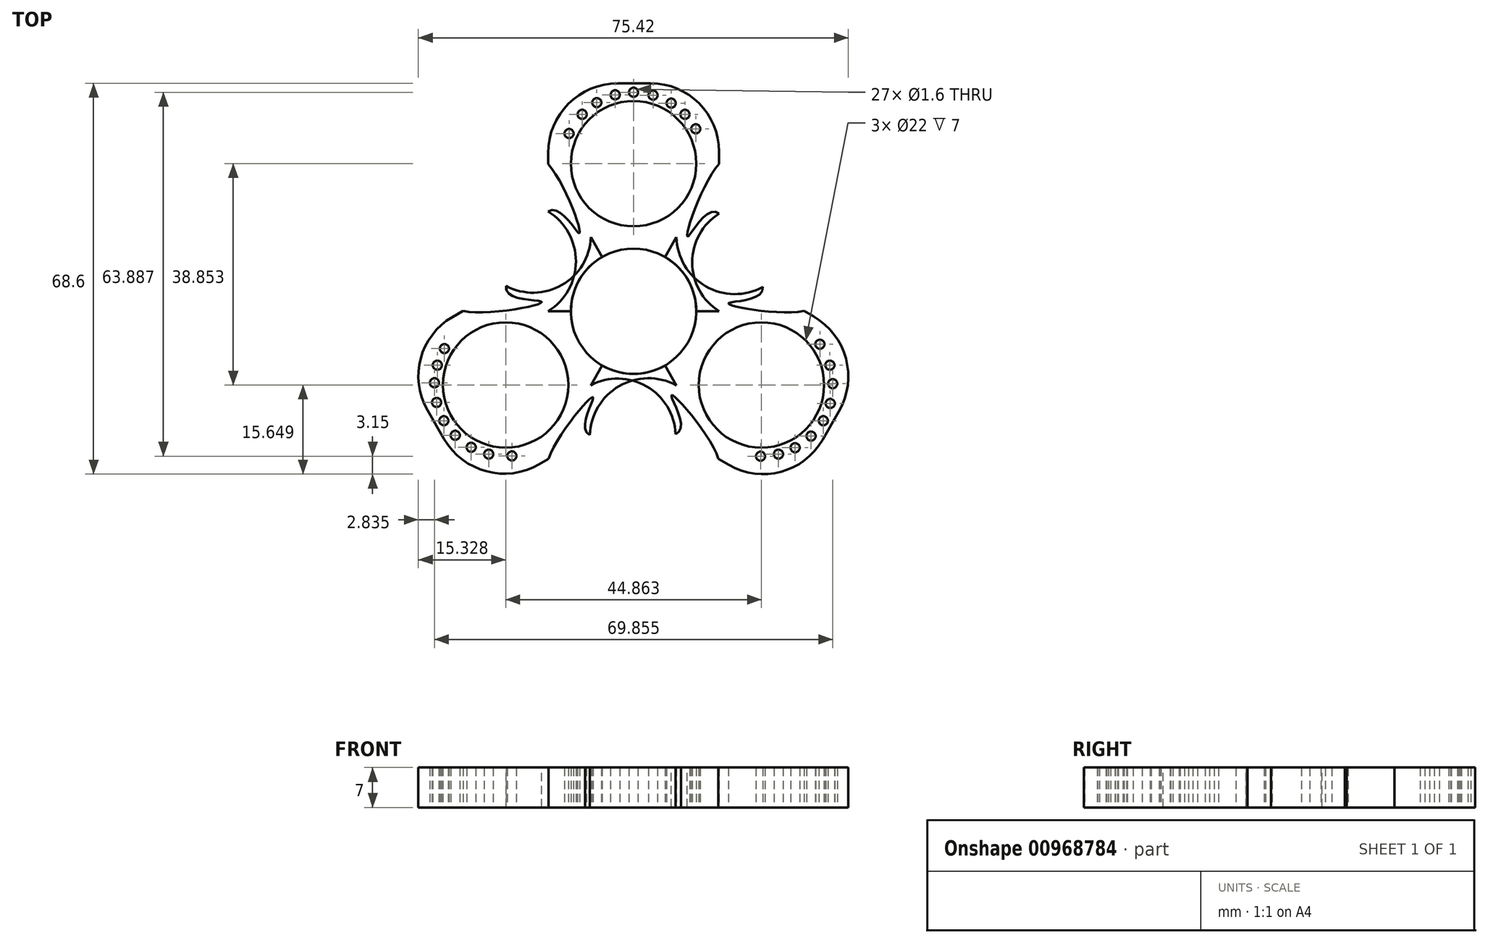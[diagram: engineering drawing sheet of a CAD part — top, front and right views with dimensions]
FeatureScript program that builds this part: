
annotation { "Feature Type Name" : "Feature", "Feature Type Description" : "" }
export const myFeature = defineFeature(function(context is Context, id is Id, definition is map)
    precondition{}
    {
        {
            var Q0;
            Q0=qCreatedBy(makeId("Top.planeOp"),FACE);
            var sketch = newSketch(context, id + "F0", { "sketchPlane" : qUnion([Q0])});
            skCircle(sketch, "E0", {"center": v(0, 0) * mm, "radius": 11 * mm});
            skLineSegment(sketch, "E1.bottom", {"start": v(0, 0) * mm, "end": v(15, 0) * mm});
            skLineSegment(sketch, "E1.top", {"start": v(0, 40) * mm, "end": v(3.02, 40) * mm});
            skLineSegment(sketch, "E1.left", {"start": v(0, 0) * mm, "end": v(0, 40) * mm});
            skLineSegment(sketch, "E1.right", {"start": v(15, 0) * mm, "end": v(15, 28.02) * mm});
            skLineSegment(sketch, "E2.bottom", {"start": v(0, 0) * mm, "end": v(-15, 0) * mm});
            skLineSegment(sketch, "E2.top", {"start": v(0, 40) * mm, "end": v(-2.77, 40) * mm});
            skLineSegment(sketch, "E2.right", {"start": v(-15, 0) * mm, "end": v(-15, 27.77) * mm});
            skLineSegment(sketch, "E3", {"start": v(0, 40) * mm, "end": v(0, 25.9) * mm});
            skCircle(sketch, "E4", {"center": v(0, 25.9) * mm, "radius": 11 * mm});
            skPoint(sketch, "E5.visualSharp", {"position": v(-15, 40) * mm});
            skArc(sketch, "E5.filletArc", {"start": v(-2.77, 40) * mm, "mid": v(-11.42, 36.42) * mm, "end": v(-15, 27.77) * mm});
            skPoint(sketch, "E6.visualSharp", {"position": v(15, 40) * mm});
            skArc(sketch, "E6.filletArc", {"start": v(15, 28.02) * mm, "mid": v(11.5, 36.5) * mm, "end": v(3.02, 40) * mm});
            skPoint(sketch, "E7.1.internal.snap0", {"position": v(-15, 13.88) * mm});
            skFitSpline(sketch, "E8", {"points": [v(-15, 25.86) * mm, v(-9.57, 13.73) * mm, v(-15, 17.51) * mm], "startDerivative": vector(15.03, -16.72) * mm, "endDerivative": vector(-15.82, -9.96) * mm});
            skFitSpline(sketch, "E9", {"points": [v(15, 25.86) * mm, v(9.53, 13.16) * mm, v(15, 17.15) * mm], "startDerivative": vector(-14.64, -15.58) * mm, "endDerivative": vector(14.98, -12.69) * mm});
            skPoint(sketch, "E10", {"position": v(15, 14) * mm});
            skCircle(sketch, "E11", {"center": v(-11.32, 31.2) * mm, "radius": 0.8 * mm});
            skCircle(sketch, "E12", {"center": v(-9.02, 34.56) * mm, "radius": 0.8 * mm});
            skCircle(sketch, "E13", {"center": v(-6.44, 36.61) * mm, "radius": 0.8 * mm});
            skCircle(sketch, "E14", {"center": v(-3.23, 37.98) * mm, "radius": 0.8 * mm});
            skCircle(sketch, "E15", {"center": v(0, 38.44) * mm, "radius": 0.8 * mm});
            skCircle(sketch, "E16", {"center": v(3.41, 37.93) * mm, "radius": 0.8 * mm});
            skCircle(sketch, "E17", {"center": v(6.6, 36.52) * mm, "radius": 0.8 * mm});
            skCircle(sketch, "E18", {"center": v(9.02, 34.56) * mm, "radius": 0.8 * mm});
            skCircle(sketch, "E19", {"center": v(10.9, 32.02) * mm, "radius": 0.8 * mm});
            skArc(sketch, "E20", {"start": v(-15, 0) * mm, "mid": v(-10.12, 8.76) * mm, "end": v(-15, 17.51) * mm});
            skArc(sketch, "E21", {"start": v(15, 17.15) * mm, "mid": v(10.27, 8.57) * mm, "end": v(15, 0) * mm});
            skLineSegment(sketch, "E22", {"start": v(-11.32, 31.2) * mm, "end": v(0, 25.9) * mm, "construction": true});
            skLineSegment(sketch, "E23", {"start": v(-9.02, 34.56) * mm, "end": v(0, 25.9) * mm, "construction": true});
            skLineSegment(sketch, "E24", {"start": v(-6.44, 36.61) * mm, "end": v(0, 25.9) * mm, "construction": true});
            skLineSegment(sketch, "E25", {"start": v(-3.23, 37.98) * mm, "end": v(0, 25.9) * mm, "construction": true});
            skLineSegment(sketch, "E26", {"start": v(0, 38.44) * mm, "end": v(0, 25.9) * mm});
            skLineSegment(sketch, "E27", {"start": v(3.41, 37.93) * mm, "end": v(0, 25.9) * mm, "construction": true});
            skLineSegment(sketch, "E28", {"start": v(6.6, 36.52) * mm, "end": v(0, 25.9) * mm, "construction": true});
            skLineSegment(sketch, "E29", {"start": v(9.02, 34.56) * mm, "end": v(0, 25.9) * mm, "construction": true});
            skLineSegment(sketch, "E30", {"start": v(10.9, 32.02) * mm, "end": v(0, 25.9) * mm, "construction": true});
            skSolve(sketch);
        }
        {
            var Q0;
            {var subQ0=sQuery(id+"F0.wireOp",EDGE,"E2.top");Q0=makeQuery(id+"F0.imprint","IMPRINT",FACE,{"disambiguationData":[TD([[makeQuery(id+"F0.imprint","IMPRINT",EDGE,{"derivedFrom":subQ0}),1.0]])]});}
            var Q1;
            {var subQ9=sQuery(id+"F0.wireOp",EDGE,"E1.top");Q1=makeQuery(id+"F0.imprint","IMPRINT",FACE,{"disambiguationData":[TD([[makeQuery(id+"F0.imprint","IMPRINT",EDGE,{"derivedFrom":subQ9}),-1.0]])]});}
            extrude(context, id + "F1", {"entities" : qUnion([Q0, Q1]), "depth" : 7 * mm, "offsetDistance" : 25 * mm});
        }
        {
            var Q0;
            Q0=qCreatedBy(makeId("Front.planeOp"),FACE);
            var sketch = newSketch(context, id + "F2", { "sketchPlane" : qUnion([Q0])});
            skLineSegment(sketch, "E31", {"start": v(0, 0) * mm, "end": v(0, 68.14) * mm});
            skSolve(sketch);
        }
        {
            var Q0;
            Q0=makeQuery(id+"F1.opExtrude","SWEPT_BODY",BODY,{"disambiguationData":[OSD([sQuery(id+"F0.wireOp",EDGE,"E0"),sQuery(id+"F0.wireOp",EDGE,"E1.bottom"),sQuery(id+"F0.wireOp",EDGE,"E1.top"),sQuery(id+"F0.wireOp",EDGE,"E1.right"),sQuery(id+"F0.wireOp",EDGE,"E2.bottom"),sQuery(id+"F0.wireOp",EDGE,"E2.top"),sQuery(id+"F0.wireOp",EDGE,"E2.right"),sQuery(id+"F0.wireOp",EDGE,"E4")])]});
            var Q1;
            Q1=sQuery(id+"F2.wireOp",EDGE,"E31");
            var Q2;
            Q2=sQuery(id+"F2.wireOp",EDGE,"E31");
            transform(context, id + "F3", {"entities" : qUnion([Q0]), "transformType" : TransformType.ROTATION, "transformAxis" : qUnion([Q2]), "angle" : 120 * degree, "makeCopy" : true});
        }
        {
            var Q0;
            Q0=makeQuery(id+"F3.opPattern","COPY",BODY,{"derivedFrom":makeQuery(id+"F1.opExtrude","SWEPT_BODY",BODY,{"disambiguationData":[OSD([sQuery(id+"F0.wireOp",EDGE,"E0"),sQuery(id+"F0.wireOp",EDGE,"E1.bottom"),sQuery(id+"F0.wireOp",EDGE,"E1.top"),sQuery(id+"F0.wireOp",EDGE,"E1.right"),sQuery(id+"F0.wireOp",EDGE,"E2.bottom"),sQuery(id+"F0.wireOp",EDGE,"E2.top"),sQuery(id+"F0.wireOp",EDGE,"E2.right"),sQuery(id+"F0.wireOp",EDGE,"E4")])]}),"instanceName":"1"});
            var Q1;
            Q1=sQuery(id+"F2.wireOp",EDGE,"E31");
            transform(context, id + "F4", {"entities" : qUnion([Q0]), "transformType" : TransformType.ROTATION, "transformAxis" : qUnion([Q1]), "angle" : 120 * degree, "makeCopy" : true});
        }
    });
